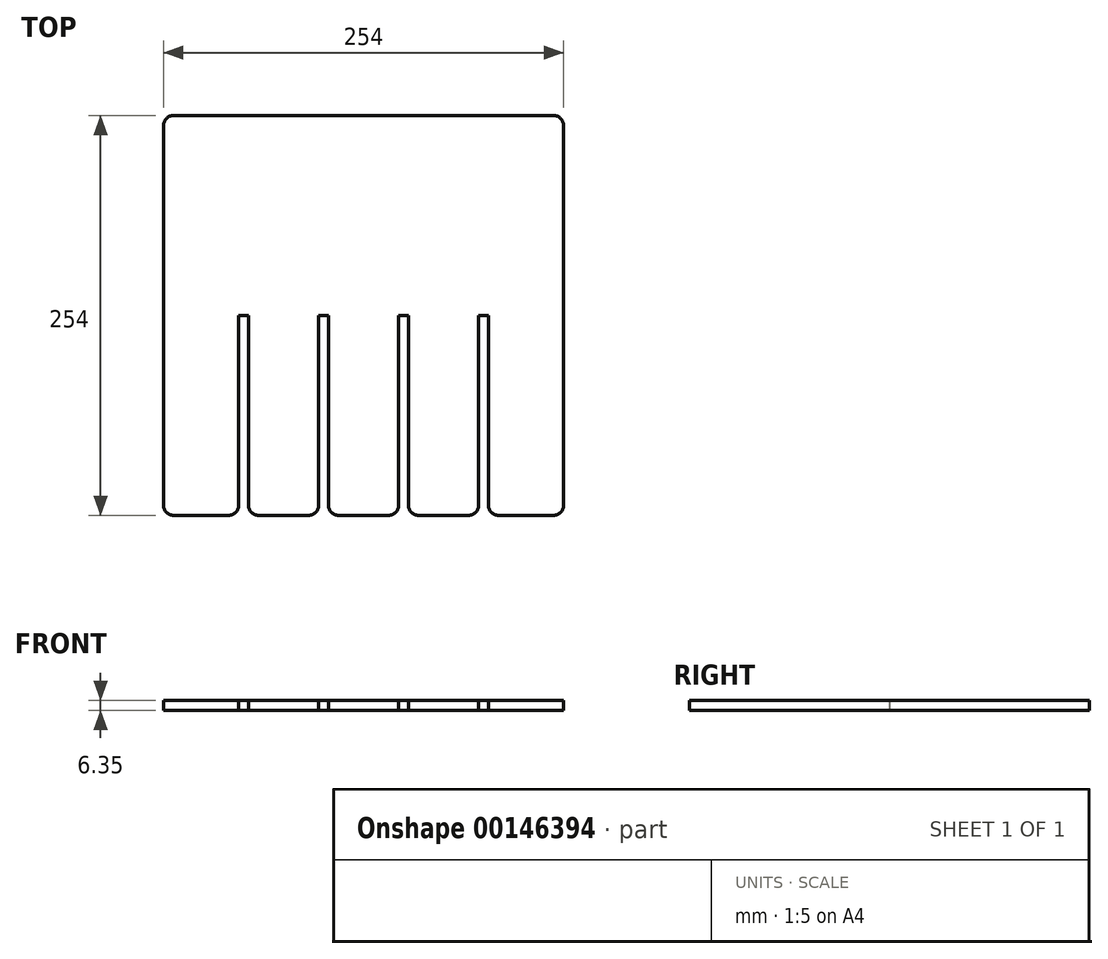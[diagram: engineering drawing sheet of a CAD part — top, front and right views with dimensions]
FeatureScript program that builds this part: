
annotation { "Feature Type Name" : "Feature", "Feature Type Description" : "" }
export const myFeature = defineFeature(function(context is Context, id is Id, definition is map)
    precondition{}
    {
        {
            var Q0;
            Q0=qCreatedBy(makeId("Top.planeOp"),FACE);
            var sketch = newSketch(context, id + "F0", { "sketchPlane" : qUnion([Q0])});
            skLineSegment(sketch, "E0.bottom", {"start": v(120.65, 127) * mm, "end": v(-120.65, 127) * mm});
            skLineSegment(sketch, "E0.top", {"start": v(120.65, -127) * mm, "end": v(85.72, -127) * mm});
            skLineSegment(sketch, "E0.left", {"start": v(127, 120.65) * mm, "end": v(127, -120.65) * mm});
            skLineSegment(sketch, "E0.right", {"start": v(-127, 120.65) * mm, "end": v(-127, -120.65) * mm});
            skPoint(sketch, "E0.middle", {"position": v(0, 0) * mm});
            skPoint(sketch, "E1.visualSharp", {"position": v(-127, 127) * mm});
            skArc(sketch, "E1.filletArc", {"start": v(-120.65, 127) * mm, "mid": v(-125.14, 125.14) * mm, "end": v(-127, 120.65) * mm});
            skPoint(sketch, "E2.visualSharp", {"position": v(127, 127) * mm});
            skArc(sketch, "E2.filletArc", {"start": v(127, 120.65) * mm, "mid": v(125.14, 125.14) * mm, "end": v(120.65, 127) * mm});
            skPoint(sketch, "E3.visualSharp", {"position": v(127, -127) * mm});
            skArc(sketch, "E3.filletArc", {"start": v(120.65, -127) * mm, "mid": v(125.14, -125.14) * mm, "end": v(127, -120.65) * mm});
            skPoint(sketch, "E4.visualSharp", {"position": v(-127, -127) * mm});
            skArc(sketch, "E4.filletArc", {"start": v(-127, -120.65) * mm, "mid": v(-125.14, -125.14) * mm, "end": v(-120.65, -127) * mm});
            skLineSegment(sketch, "E5", {"start": v(-120.65, -127) * mm, "end": v(-85.73, -127) * mm});
            skLineSegment(sketch, "E6", {"start": v(-66.68, -127) * mm, "end": v(-34.93, -127) * mm});
            skLineSegment(sketch, "E7", {"start": v(34.92, -127) * mm, "end": v(66.67, -127) * mm});
            skLineSegment(sketch, "E8", {"start": v(85.72, -127) * mm, "end": v(120.65, -127) * mm});
            skLineSegment(sketch, "E9.0", {"start": v(-73.03, -120.65) * mm, "end": v(-73.03, 0) * mm});
            skLineSegment(sketch, "E10.0", {"start": v(-79.38, -120.65) * mm, "end": v(-79.38, 0) * mm});
            skLineSegment(sketch, "E11.0", {"start": v(-22.23, -120.65) * mm, "end": v(-22.23, 0) * mm});
            skLineSegment(sketch, "E12.0", {"start": v(-28.58, -120.65) * mm, "end": v(-28.58, 0) * mm});
            skLineSegment(sketch, "E13.0", {"start": v(28.57, -120.65) * mm, "end": v(28.57, 0) * mm});
            skLineSegment(sketch, "E14.0", {"start": v(22.22, -120.65) * mm, "end": v(22.22, 0) * mm});
            skLineSegment(sketch, "E15.0", {"start": v(79.37, -120.65) * mm, "end": v(79.37, 0) * mm});
            skLineSegment(sketch, "E16.0", {"start": v(73.02, -120.65) * mm, "end": v(73.02, 0) * mm});
            skLineSegment(sketch, "E17", {"start": v(-79.38, 0) * mm, "end": v(-73.03, 0) * mm});
            skLineSegment(sketch, "E18", {"start": v(-28.58, 0) * mm, "end": v(-22.23, 0) * mm});
            skLineSegment(sketch, "E19", {"start": v(22.22, 0) * mm, "end": v(28.57, 0) * mm});
            skLineSegment(sketch, "E20", {"start": v(73.02, 0) * mm, "end": v(79.37, 0) * mm});
            skPoint(sketch, "E21.end.orphan", {"position": v(-76.2, 0) * mm});
            skPoint(sketch, "E22.end.orphan", {"position": v(-25.4, 0) * mm});
            skPoint(sketch, "E23.end.orphan", {"position": v(25.4, 0) * mm});
            skPoint(sketch, "E24.end.orphan", {"position": v(76.2, 0) * mm});
            skLineSegment(sketch, "E25.trimOffspring", {"start": v(-34.93, -127) * mm, "end": v(-66.68, -127) * mm});
            skLineSegment(sketch, "E26.trimOffspring", {"start": v(15.87, -127) * mm, "end": v(-15.88, -127) * mm});
            skLineSegment(sketch, "E27.trimOffspring", {"start": v(66.67, -127) * mm, "end": v(34.92, -127) * mm});
            skPoint(sketch, "E28.visualSharp", {"position": v(-79.38, -127) * mm});
            skArc(sketch, "E28.filletArc", {"start": v(-85.73, -127) * mm, "mid": v(-81.23, -125.14) * mm, "end": v(-79.38, -120.65) * mm});
            skPoint(sketch, "E29.visualSharp", {"position": v(-73.03, -127) * mm});
            skArc(sketch, "E29.filletArc", {"start": v(-73.03, -120.65) * mm, "mid": v(-71.17, -125.14) * mm, "end": v(-66.68, -127) * mm});
            skPoint(sketch, "E30.visualSharp", {"position": v(-28.58, -127) * mm});
            skArc(sketch, "E30.filletArc", {"start": v(-34.93, -127) * mm, "mid": v(-30.43, -125.14) * mm, "end": v(-28.58, -120.65) * mm});
            skPoint(sketch, "E31.visualSharp", {"position": v(-22.23, -127) * mm});
            skArc(sketch, "E31.filletArc", {"start": v(-22.23, -120.65) * mm, "mid": v(-20.37, -125.14) * mm, "end": v(-15.88, -127) * mm});
            skPoint(sketch, "E32.visualSharp", {"position": v(28.57, -127) * mm});
            skArc(sketch, "E32.filletArc", {"start": v(28.57, -120.65) * mm, "mid": v(30.43, -125.14) * mm, "end": v(34.92, -127) * mm});
            skPoint(sketch, "E33.visualSharp", {"position": v(22.22, -127) * mm});
            skArc(sketch, "E33.filletArc", {"start": v(15.87, -127) * mm, "mid": v(20.37, -125.14) * mm, "end": v(22.22, -120.65) * mm});
            skPoint(sketch, "E34.visualSharp", {"position": v(73.02, -127) * mm});
            skArc(sketch, "E34.filletArc", {"start": v(66.67, -127) * mm, "mid": v(71.17, -125.14) * mm, "end": v(73.02, -120.65) * mm});
            skPoint(sketch, "E35.visualSharp", {"position": v(79.37, -127) * mm});
            skArc(sketch, "E35.filletArc", {"start": v(79.37, -120.65) * mm, "mid": v(81.23, -125.14) * mm, "end": v(85.72, -127) * mm});
            skSolve(sketch);
        }
        {
            var Q0;
            Q0 = qSketchRegion(id + "F0", true);
            extrude(context, id + "F1", {"entities" : qUnion([Q0]), "depth" : 6.35 * mm});
        }
    });
